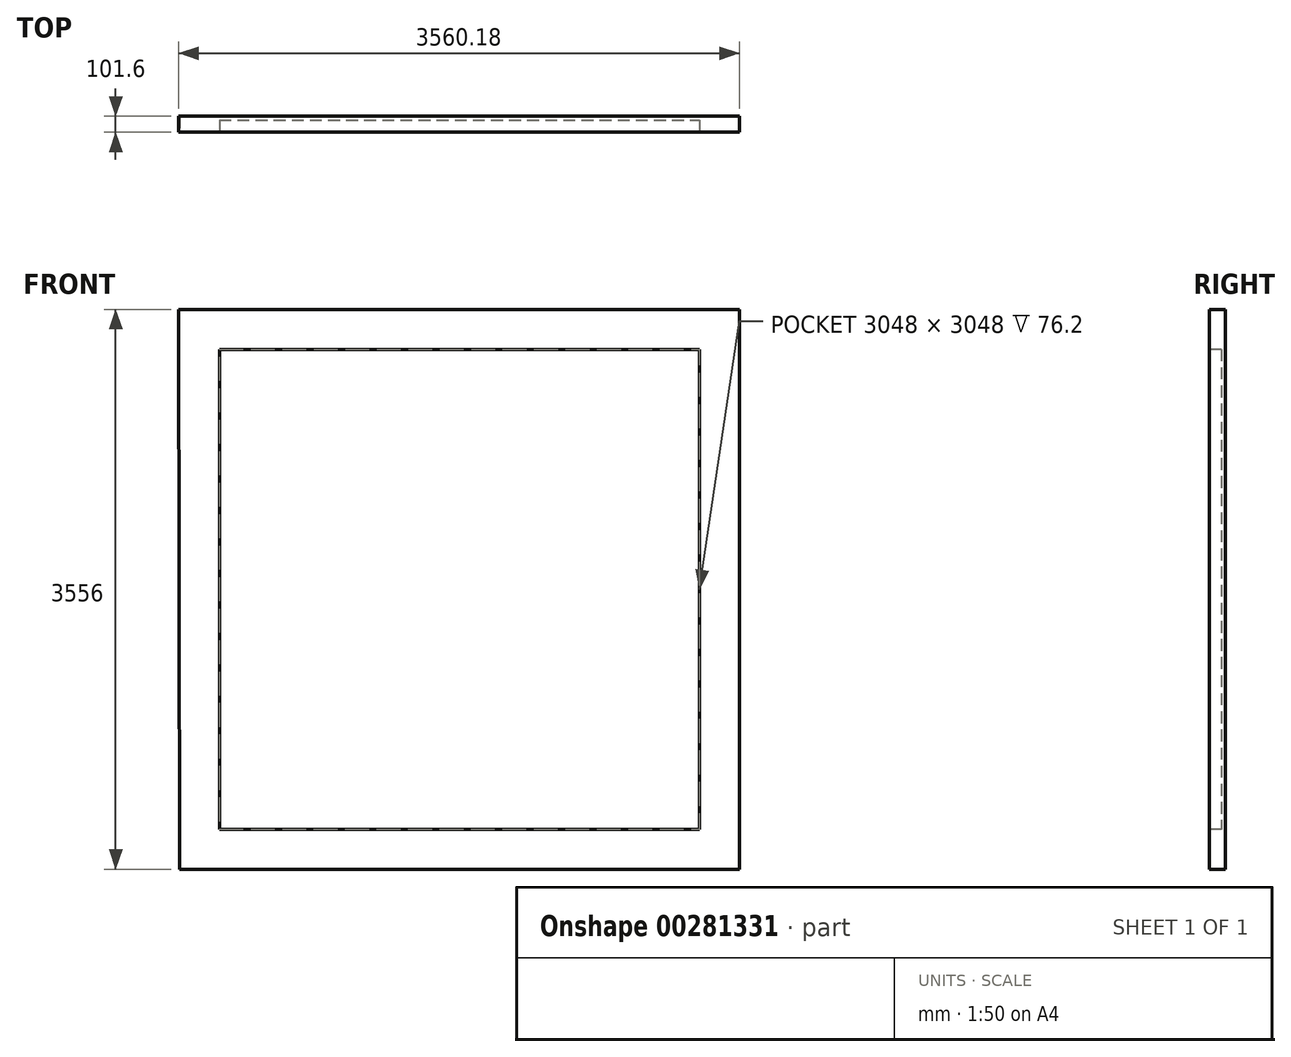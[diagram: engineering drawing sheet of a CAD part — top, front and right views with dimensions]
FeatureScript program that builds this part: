
annotation { "Feature Type Name" : "Feature", "Feature Type Description" : "" }
export const myFeature = defineFeature(function(context is Context, id is Id, definition is map)
    precondition{}
    {
        {
            var Q0;
            Q0=qCreatedBy(makeId("Front.planeOp"),FACE);
            var sketch = newSketch(context, id + "F0", { "sketchPlane" : qUnion([Q0])});
            skLineSegment(sketch, "E0", {"start": v(3069.87, -6311.02) * mm, "end": v(6117.87, -6311.02) * mm});
            skLineSegment(sketch, "E1", {"start": v(2815.87, -6565.02) * mm, "end": v(6371.87, -6565.02) * mm});
            skLineSegment(sketch, "E2", {"start": v(6117.87, -6311.02) * mm, "end": v(6117.87, -3263.02) * mm});
            skLineSegment(sketch, "E3", {"start": v(6371.87, -6565.02) * mm, "end": v(6371.87, -3009.02) * mm});
            skLineSegment(sketch, "E4", {"start": v(6117.87, -3263.02) * mm, "end": v(3069.87, -3263.02) * mm});
            skLineSegment(sketch, "E5", {"start": v(6367.69, -3009.02) * mm, "end": v(2811.69, -3009.02) * mm});
            skLineSegment(sketch, "E6", {"start": v(3069.87, -3263.02) * mm, "end": v(3069.87, -6311.02) * mm});
            skLineSegment(sketch, "E7", {"start": v(2811.69, -3009.02) * mm, "end": v(2815.87, -6565.02) * mm});
            skLineSegment(sketch, "E8", {"start": v(6371.87, -3009.02) * mm, "end": v(2811.69, -3009.02) * mm});
            skSolve(sketch);
        }
        {
            var Q0;
            Q0=makeQuery(id+"F0.imprint","IMPRINT",FACE,{"disambiguationData":[TD([[makeQuery(id+"F0.imprint","IMPRINT",EDGE,{"derivedFrom":sQuery(id+"F0.wireOp",EDGE,"E0")}),-1.0]])]});
            var Q1;
            Q1=makeQuery(id+"F0.imprint","IMPRINT",FACE,{"disambiguationData":[TD([[makeQuery(id+"F0.imprint","IMPRINT",EDGE,{"derivedFrom":sQuery(id+"F0.wireOp",EDGE,"E0")}),1.0]])]});
            extrude(context, id + "F1", {"entities" : qUnion([Q0, Q1]), "oppositeDirection" : true, "depth" : 101.6 * mm});
        }
        {
            var Q0;
            Q0=makeQuery(id+"F0.imprint","IMPRINT",FACE,{"disambiguationData":[TD([[makeQuery(id+"F0.imprint","IMPRINT",EDGE,{"derivedFrom":sQuery(id+"F0.wireOp",EDGE,"E0")}),1.0]])]});
            extrude(context, id + "F2", {"entities" : qUnion([Q0]), "operationType" : NewBodyOperationType.REMOVE, "oppositeDirection" : true, "depth" : 76.2 * mm});
        }
    });
